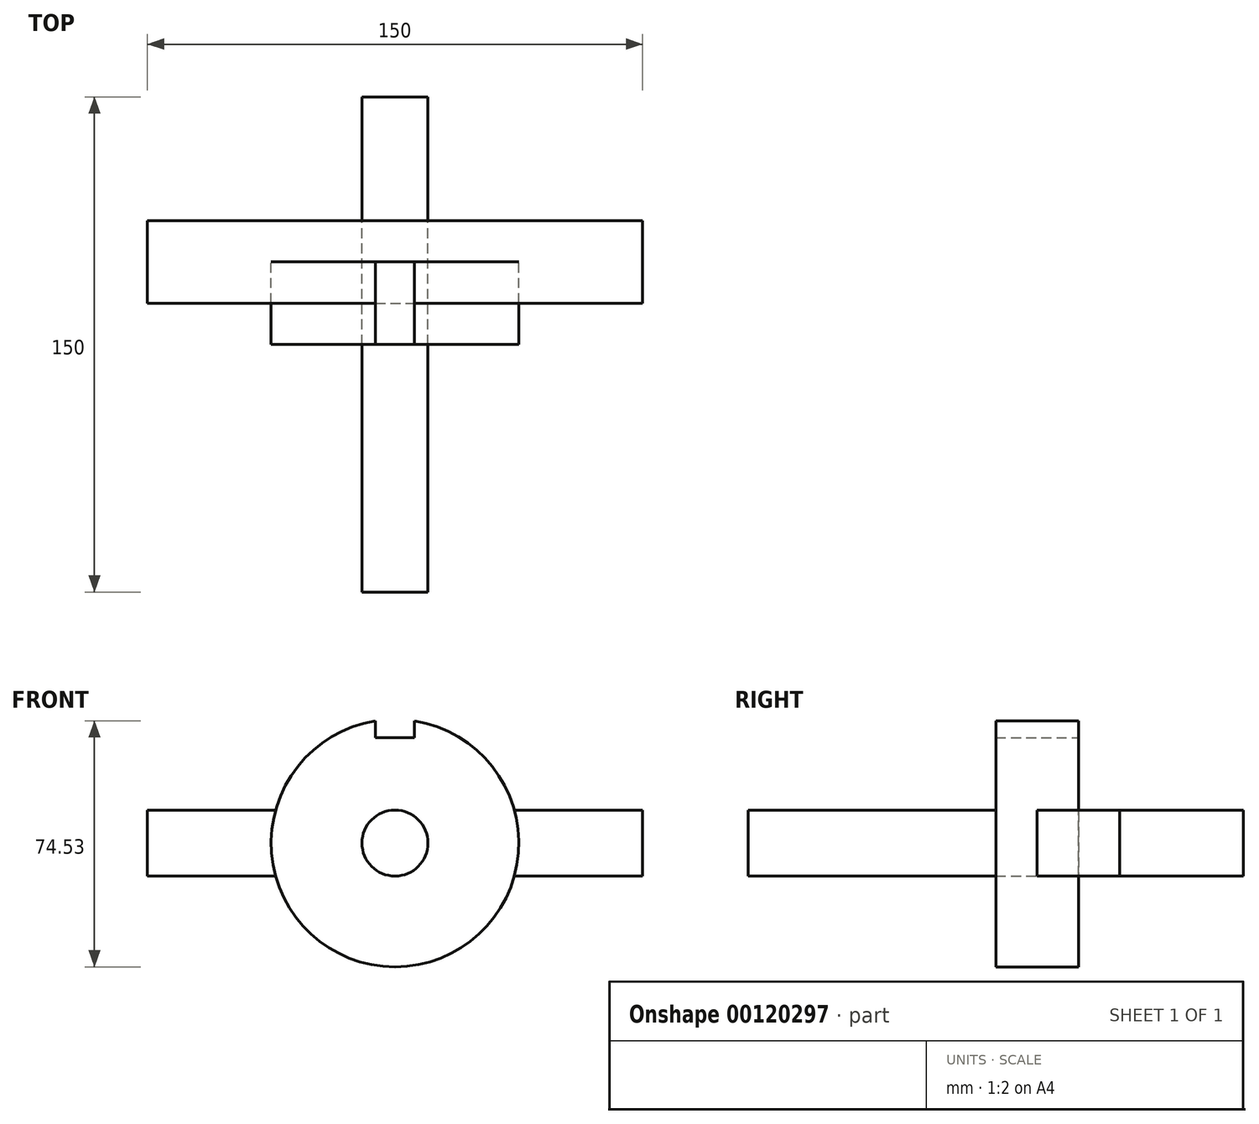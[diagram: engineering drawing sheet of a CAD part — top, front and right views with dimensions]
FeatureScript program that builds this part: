
annotation { "Feature Type Name" : "Feature", "Feature Type Description" : "" }
export const myFeature = defineFeature(function(context is Context, id is Id, definition is map)
    precondition{}
    {
        {
            var Q0;
            Q0=qCreatedBy(makeId("Front.planeOp"),FACE);
            var sketch = newSketch(context, id + "F0", { "sketchPlane" : qUnion([Q0])});
            skCircle(sketch, "E0", {"center": v(0, 0) * mm, "radius": 37.5 * mm});
            skLineSegment(sketch, "E1.bottom", {"start": v(5.92, 31.9) * mm, "end": v(-5.92, 31.9) * mm});
            skLineSegment(sketch, "E1.top", {"start": v(5.92, 43.1) * mm, "end": v(-5.92, 43.1) * mm});
            skLineSegment(sketch, "E1.left", {"start": v(5.92, 31.9) * mm, "end": v(5.92, 43.1) * mm});
            skLineSegment(sketch, "E1.right", {"start": v(-5.92, 31.9) * mm, "end": v(-5.92, 43.1) * mm});
            skPoint(sketch, "E1.middle", {"position": v(0, 37.5) * mm});
            skCircle(sketch, "E2", {"center": v(0, 0) * mm, "radius": 10 * mm});
            skSolve(sketch);
        }
        {
            var Q0;
            {var subQ5=sQuery(id+"F0.wireOp",EDGE,"E1.bottom");Q0=makeQuery(id+"F0.imprint","IMPRINT",FACE,{"disambiguationData":[TD([[makeQuery(id+"F0.imprint","IMPRINT",EDGE,{"derivedFrom":subQ5}),1.0]])]});}
            extrude(context, id + "F1", {"entities" : qUnion([Q0]), "depth" : 25 * mm});
        }
        {
            var Q0;
            Q0=makeQuery(id+"F0.imprint","IMPRINT",FACE,{"disambiguationData":[TD([[makeQuery(id+"F0.imprint","IMPRINT",EDGE,{"derivedFrom":sQuery(id+"F0.wireOp",EDGE,"E2")}),1.0]])]});
            extrude(context, id + "F2", {"entities" : qUnion([Q0]), "depth" : 100 * mm, "hasSecondDirection" : true, "secondDirectionOppositeDirection" : true, "secondDirectionDepth" : 50 * mm});
        }
        {
            var Q0;
            Q0=qCreatedBy(makeId("Front.planeOp"),FACE);
            var sketch = newSketch(context, id + "F3", { "sketchPlane" : qUnion([Q0])});
            skLineSegment(sketch, "E3.bottom", {"start": v(-75, 10) * mm, "end": v(75, 10) * mm});
            skLineSegment(sketch, "E3.top", {"start": v(-75, -10) * mm, "end": v(75, -10) * mm});
            skLineSegment(sketch, "E3.left", {"start": v(-75, 10) * mm, "end": v(-75, -10) * mm});
            skLineSegment(sketch, "E3.right", {"start": v(75, 10) * mm, "end": v(75, -10) * mm});
            skPoint(sketch, "E3.middle", {"position": v(0, 0) * mm});
            skSolve(sketch);
        }
        {
            var Q0;
            Q0=qSketchRegion(id+"F3",true);
            extrude(context, id + "F4", {"entities" : qUnion([Q0]), "endBound" : BoundingType.SYMMETRIC, "depth" : 25 * mm});
        }
    });
